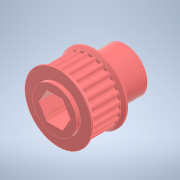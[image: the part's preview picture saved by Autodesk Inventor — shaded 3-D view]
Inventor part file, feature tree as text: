
AUTODESK INVENTOR PART (.ipt)
format: ipt  version: 2022.3 (Build 263350000, 350)  size: 331,776 bytes
history: native  units: in
note: dims shown in document units (in); Inventor stores cm internally (conversion verified against a paired STEP export)
features: extrude x8, sketch x7, mirror x2, chamfer x2, other x1, fillet x1, pattern_circular x1, projected_geometry x1
ambient origin geometry x8: Origin, YZ Plane, XZ Plane, XY Plane, X Axis, Y Axis, Z Axis, Center Point
bodies: Solid1 (feature_tree)
feature tree (23):
  other  "Hex Bore"
  extrude  "HTD Base"  Depth=0.3937in TaperAngle=0.0deg
  extrude  "HTD Flange"  Depth=0.0591in
  mirror  "HTD Flanges"
  chamfer  "HTD Flange Chamfer"  Distance=0.0787in Angle=45.0deg
  extrude  "GT2 Base"  TaperAngle=0.0deg  [1 undecoded]
  extrude  "GT2 Base Tooth"  TaperAngle=0.0deg  [1 undecoded]
  fillet  "GT2 Base Tooth pt. 2"  Radius=0.8723in
  pattern_circular  "GT2 Teeth"  [2 undecoded]
  extrude  "GT2 Flange"  Depth=0.5638in
  mirror  "GT2 Flanges"
  chamfer  "GT2 Flange Chamfer"  Distance=0.0075in
  extrude  "Circle Bore"  TaperAngle=0.0deg  [1 undecoded]
  sketch  "Sketch9"  dims[d25=0.3937in d26=0.0in d27=0.0727in d28=0.0075in d29=0.0in d30=0.0in d31=0.0118in d32=9.4488in d33=360.0deg d35=0.0394in d36=0.0591in d37=0.0in d38=0.0394in d39=0.0787in d40=45.0deg d41=0.625in d42=0.4375in d43=0.0in d44=0.5638in d45=0.0in]
  extrude  "Extrusion10"  Depth=0.0118in
  extrude  "Extrusion9"  Depth=0.5638in
  sketch  "Sketch1"  dims[d0=1.4588in d1=0.3937in d2=0.0in]
  sketch  "Sketch4"  dims[d12=0.0394in d13=0.0591in]
  sketch  "Sketch5"  dims[d14=0.0in]
  sketch  "Sketch6"  dims[d15=0.0394in d16=0.0787in d17=45.0deg]
  sketch  "Sketch7"  dims[d18=0.385in d19=0.0in d20=0.0in]
  sketch  "Sketch8"  dims[d21=0.385in d22=0.0in d23=0.0in d24=0.8723in]
  projected_geometry  "Projected Loop1"
note: 5 required parameter values undecoded (feature->parameter linkage not recoverable at this tier; creation-order binding heuristic only, values carry confidence <= 0.55)
